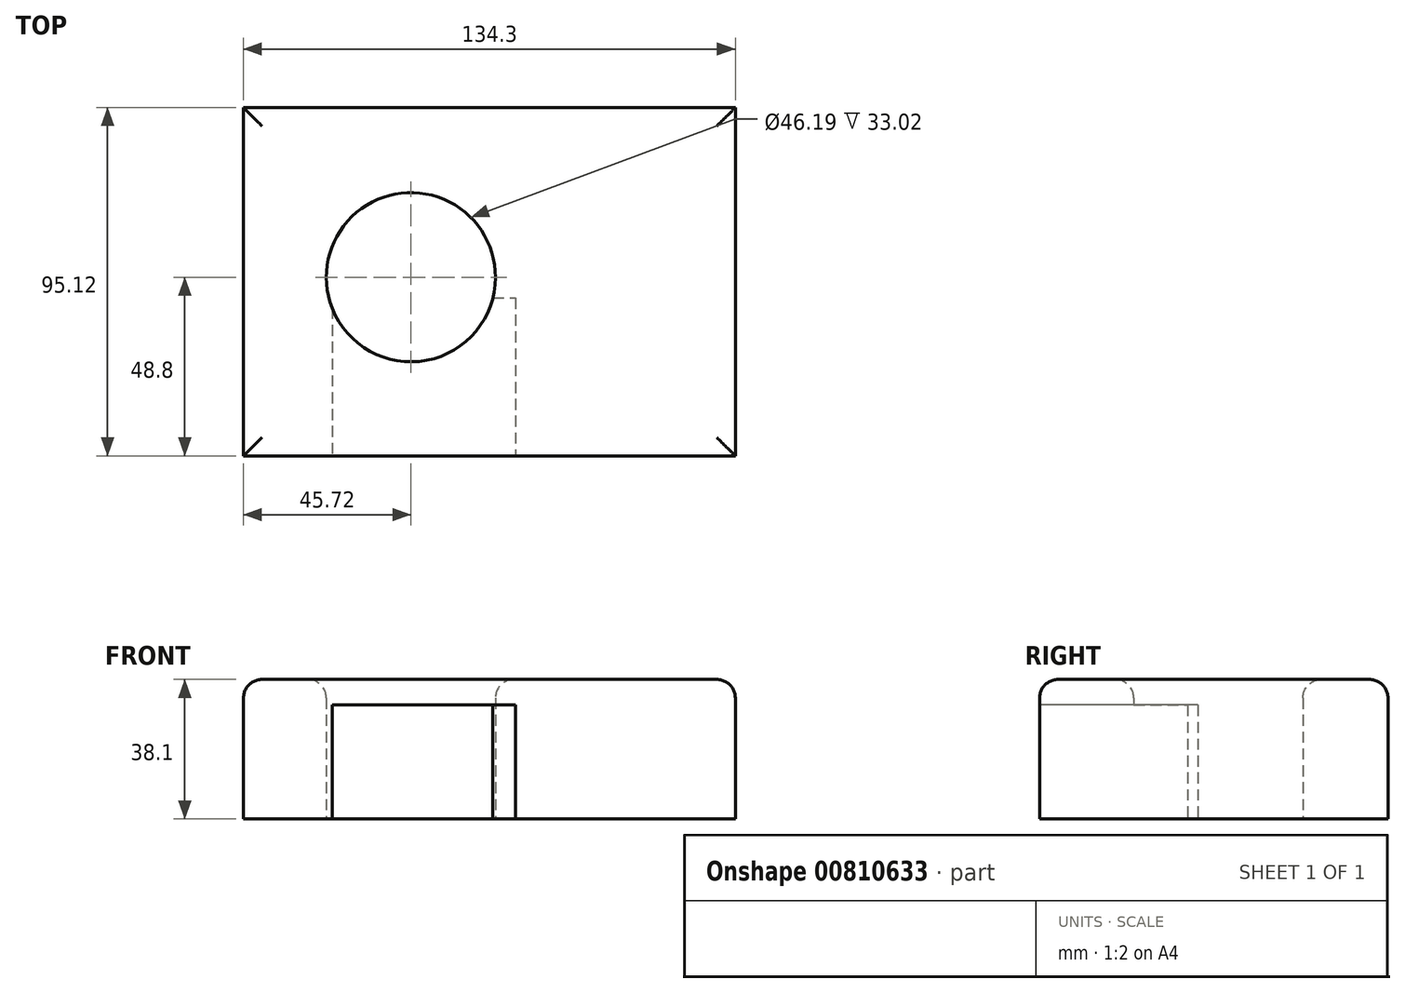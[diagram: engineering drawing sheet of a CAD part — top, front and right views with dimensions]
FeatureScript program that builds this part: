
annotation { "Feature Type Name" : "Feature", "Feature Type Description" : "" }
export const myFeature = defineFeature(function(context is Context, id is Id, definition is map)
    precondition{}
    {
        {
            var Q0;
            Q0=qCreatedBy(makeId("Top.planeOp"),FACE);
            var sketch = newSketch(context, id + "F0", { "sketchPlane" : qUnion([Q0])});
            skCircle(sketch, "E0", {"center": v(0, 0) * mm, "radius": 23.1 * mm});
            skSolve(sketch);
        }
        {
            var Q0;
            Q0=makeQuery(id+"F0.imprint","IMPRINT",FACE,{"disambiguationData":[TD([[makeQuery(id+"F0.imprint","IMPRINT",EDGE,{"derivedFrom":sQuery(id+"F0.wireOp",EDGE,"E0")}),1.0]])]});
            var sketch = newSketch(context, id + "F1", { "sketchPlane" : qUnion([Q0])});
            skLineSegment(sketch, "E1.bottom", {"start": v(-45.72, 46.32) * mm, "end": v(88.58, 46.32) * mm});
            skLineSegment(sketch, "E1.top", {"start": v(-45.72, -48.8) * mm, "end": v(88.58, -48.8) * mm});
            skLineSegment(sketch, "E1.left", {"start": v(-45.72, 46.32) * mm, "end": v(-45.72, -48.8) * mm});
            skLineSegment(sketch, "E1.right", {"start": v(88.58, 46.32) * mm, "end": v(88.58, -48.8) * mm});
            skSolve(sketch);
        }
        {
            var Q0;
            Q0=makeQuery(id+"F1.imprint","IMPRINT",FACE,{"disambiguationData":[TD([[makeQuery(id+"F1.imprint","IMPRINT",EDGE,{"derivedFrom":sQuery(id+"F1.wireOp",EDGE,"E1.bottom")}),-1.0]])]});
            extrude(context, id + "F2", {"entities" : qUnion([Q0]), "depth" : 38.1 * mm, "offsetDistance" : 25.4 * mm});
        }
        {
            var Q0;
            Q0=makeQuery(id+"F2.opExtrude","SWEPT_FACE",FACE,{"disambiguationData":[OSD([sQuery(id+"F1.wireOp",EDGE,"E1.top")])]});
            var sketch = newSketch(context, id + "F3", { "sketchPlane" : qUnion([Q0])});
            skLineSegment(sketch, "E2.bottom", {"start": v(-21.5, 31.09) * mm, "end": v(28.61, 31.09) * mm});
            skLineSegment(sketch, "E2.top", {"start": v(-21.5, 0) * mm, "end": v(28.61, 0) * mm});
            skLineSegment(sketch, "E2.left", {"start": v(-21.5, 31.09) * mm, "end": v(-21.5, 0) * mm});
            skLineSegment(sketch, "E2.right", {"start": v(28.61, 31.09) * mm, "end": v(28.61, 0) * mm});
            skSolve(sketch);
        }
        {
            var Q0;
            Q0=makeQuery(id+"F3.imprint","IMPRINT",FACE,{"disambiguationData":[TD([[makeQuery(id+"F3.imprint","IMPRINT",EDGE,{"derivedFrom":sQuery(id+"F3.wireOp",EDGE,"E2.bottom")}),-1.0]])]});
            extrude(context, id + "F4", {"entities" : qUnion([Q0]), "operationType" : NewBodyOperationType.REMOVE, "oppositeDirection" : true, "depth" : 43.18 * mm, "offsetDistance" : 25.4 * mm});
        }
        {
            var Q0;
            Q0=makeQuery(id+"F2.opExtrude","CAP_FACE",FACE,{"disambiguationData":[OSD([sQuery(id+"F0.wireOp",EDGE,"E0"),sQuery(id+"F1.wireOp",EDGE,"E1.bottom"),sQuery(id+"F1.wireOp",EDGE,"E1.top"),sQuery(id+"F1.wireOp",EDGE,"E1.left"),sQuery(id+"F1.wireOp",EDGE,"E1.right")])],"isStart":false});
            fillet(context, id + "F5", {"entities" : qUnion([Q0]), "radius" : 5.08 * mm, "tangentPropagation" : true, "allowEdgeOverflow" : false});
        }
    });
